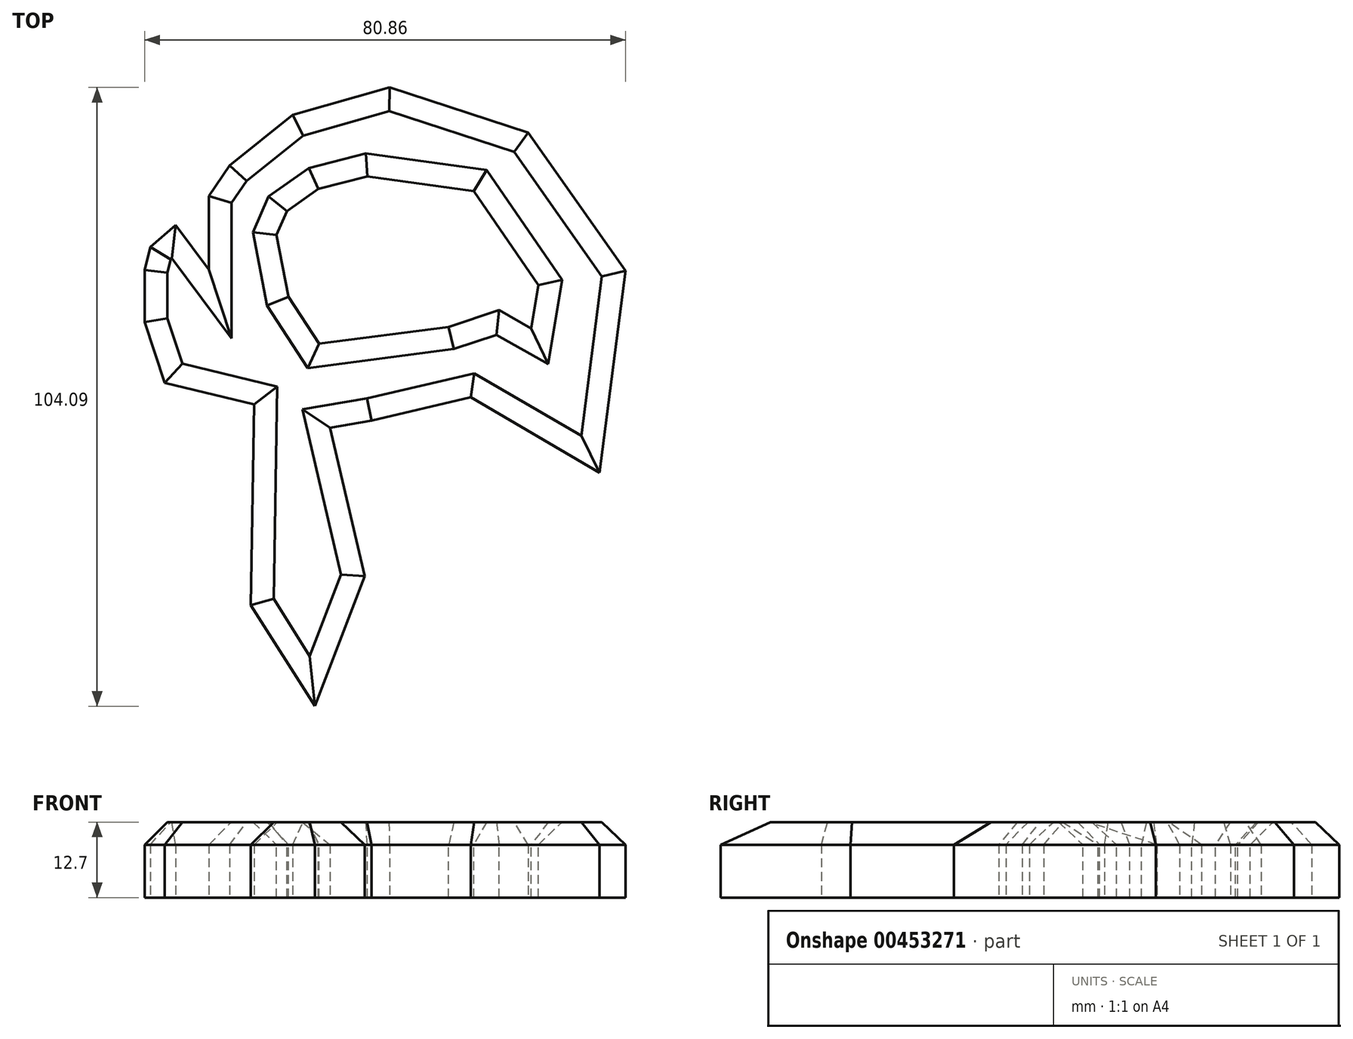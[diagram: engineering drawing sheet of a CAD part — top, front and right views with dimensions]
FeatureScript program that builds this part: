
annotation { "Feature Type Name" : "Feature", "Feature Type Description" : "" }
export const myFeature = defineFeature(function(context is Context, id is Id, definition is map)
    precondition{}
    {
        {
            var Q0;
            Q0=qCreatedBy(makeId("Top.planeOp"),FACE);
            var sketch = newSketch(context, id + "F0", { "sketchPlane" : qUnion([Q0])});
            skLineSegment(sketch, "E0", {"start": v(26.1, -25.38) * mm, "end": v(11.06, -21.75) * mm});
            skLineSegment(sketch, "E1", {"start": v(72.2, 20.34) * mm, "end": v(88.53, -2.88) * mm});
            skLineSegment(sketch, "E2", {"start": v(88.53, -2.88) * mm, "end": v(84.18, -36.85) * mm});
            skLineSegment(sketch, "E3", {"start": v(84.18, -36.85) * mm, "end": v(62.5, -24.2) * mm});
            skLineSegment(sketch, "E4", {"start": v(62.5, -24.2) * mm, "end": v(45.8, -28.13) * mm});
            skLineSegment(sketch, "E5", {"start": v(38.83, -29.3) * mm, "end": v(44.69, -54.3) * mm});
            skLineSegment(sketch, "E6", {"start": v(44.69, -54.3) * mm, "end": v(36.27, -76.15) * mm});
            skLineSegment(sketch, "E7", {"start": v(36.27, -76.15) * mm, "end": v(25.52, -59.19) * mm});
            skLineSegment(sketch, "E8", {"start": v(25.52, -59.19) * mm, "end": v(26.1, -25.38) * mm});
            skLineSegment(sketch, "E9", {"start": v(48.9, 27.94) * mm, "end": v(72.2, 20.34) * mm});
            skLineSegment(sketch, "E10", {"start": v(38.83, -29.3) * mm, "end": v(45.8, -28.13) * mm});
            skLineSegment(sketch, "E11", {"start": v(18.44, -2.73) * mm, "end": v(18.44, 9.7) * mm});
            skLineSegment(sketch, "E12", {"start": v(18.44, 9.7) * mm, "end": v(21.97, 14.81) * mm});
            skLineSegment(sketch, "E13", {"start": v(21.97, 14.81) * mm, "end": v(32.52, 23.32) * mm});
            skLineSegment(sketch, "E14", {"start": v(32.52, 23.32) * mm, "end": v(48.9, 27.94) * mm});
            skLineSegment(sketch, "E15", {"start": v(11.06, -21.75) * mm, "end": v(7.67, -11.52) * mm});
            skLineSegment(sketch, "E16", {"start": v(7.67, -11.52) * mm, "end": v(7.67, -2.75) * mm});
            skLineSegment(sketch, "E17", {"start": v(7.67, -2.75) * mm, "end": v(8.6, 1.1) * mm});
            skLineSegment(sketch, "E18", {"start": v(8.6, 1.1) * mm, "end": v(12.87, 4.8) * mm});
            skLineSegment(sketch, "E19", {"start": v(12.87, 4.8) * mm, "end": v(18.44, -2.73) * mm});
            skSolve(sketch);
        }
        {
            var Q0;
            Q0=qSketchRegion(id+"FpxrbdjMyEjlgeR_4",true);
            var Q1;
            Q1=qSketchRegion(id+"FhSuuO6UR1XzC2C_4",true);
            var Q2;
            Q2=qSketchRegion(id+"FTeMgZZDWwlIoI5_4",true);
            var Q3;
            Q3=qSketchRegion(id+"F0",true);
            extrude(context, id + "F1", {"entities" : qUnion([Q0, Q1, Q2, Q3]), "depth" : 12.7 * mm});
        }
        {
            var Q0;
            Q0=makeQuery(id+"F1.opExtrude","CAP_FACE",FACE,{"disambiguationData":[OSD([sQuery(id+"F0.wireOp",EDGE,"8451e0b5-f0a6-4988-9fe2-21164b1bf978"),sQuery(id+"F0.wireOp",EDGE,"E0"),sQuery(id+"F0.wireOp",EDGE,"0a3b12fb-e389-427a-acdd-57af8a90724c"),sQuery(id+"F0.wireOp",EDGE,"E1"),sQuery(id+"F0.wireOp",EDGE,"E2"),sQuery(id+"F0.wireOp",EDGE,"E3"),sQuery(id+"F0.wireOp",EDGE,"E4"),sQuery(id+"F0.wireOp",EDGE,"E5"),sQuery(id+"F0.wireOp",EDGE,"E6"),sQuery(id+"F0.wireOp",EDGE,"E7")])],"isStart":false});
            var sketch = newSketch(context, id + "F2", { "sketchPlane" : qUnion([Q0])});
            skLineSegment(sketch, "E20", {"start": v(31.84, -7.29) * mm, "end": v(36.99, -15.17) * mm});
            skLineSegment(sketch, "E21", {"start": v(36.99, -15.17) * mm, "end": v(58.8, -12.34) * mm});
            skLineSegment(sketch, "E22", {"start": v(73.88, -5.31) * mm, "end": v(63, 10.51) * mm});
            skLineSegment(sketch, "E23", {"start": v(63, 10.51) * mm, "end": v(45.1, 12.96) * mm});
            skLineSegment(sketch, "E24", {"start": v(73.88, -5.31) * mm, "end": v(72.69, -12.6) * mm});
            skLineSegment(sketch, "E25", {"start": v(72.69, -12.6) * mm, "end": v(67.26, -9.52) * mm});
            skLineSegment(sketch, "E26", {"start": v(67.26, -9.52) * mm, "end": v(58.8, -12.34) * mm});
            skLineSegment(sketch, "E27", {"start": v(31.84, -7.29) * mm, "end": v(29.82, 3.15) * mm});
            skLineSegment(sketch, "E28", {"start": v(29.82, 3.15) * mm, "end": v(31.57, 7.12) * mm});
            skLineSegment(sketch, "E29", {"start": v(31.57, 7.12) * mm, "end": v(36.89, 10.87) * mm});
            skLineSegment(sketch, "E30", {"start": v(36.89, 10.87) * mm, "end": v(45.1, 12.96) * mm});
            skSolve(sketch);
        }
        {
            var Q0;
            Q0=qSketchRegion(id+"F2",true);
            extrude(context, id + "F3", {"entities" : qUnion([Q0]), "operationType" : NewBodyOperationType.REMOVE, "endBound" : BoundingType.THROUGH_ALL, "oppositeDirection" : true, "depth" : 25.4 * mm});
        }
        {
            var Q0;
            Q0=makeQuery(id+"F1.opExtrude","CAP_FACE",FACE,{"disambiguationData":[OSD([sQuery(id+"F0.wireOp",EDGE,"8451e0b5-f0a6-4988-9fe2-21164b1bf978"),sQuery(id+"F0.wireOp",EDGE,"E0"),sQuery(id+"F0.wireOp",EDGE,"0a3b12fb-e389-427a-acdd-57af8a90724c"),sQuery(id+"F0.wireOp",EDGE,"E1"),sQuery(id+"F0.wireOp",EDGE,"E2"),sQuery(id+"F0.wireOp",EDGE,"E3"),sQuery(id+"F0.wireOp",EDGE,"E4"),sQuery(id+"F0.wireOp",EDGE,"E5"),sQuery(id+"F0.wireOp",EDGE,"E6"),sQuery(id+"F0.wireOp",EDGE,"E7")])],"isStart":false});
            chamfer(context, id + "F4", {"entities" : qUnion([Q0]), "width" : 3.8 * mm, "tangentPropagation" : true});
        }
    });
